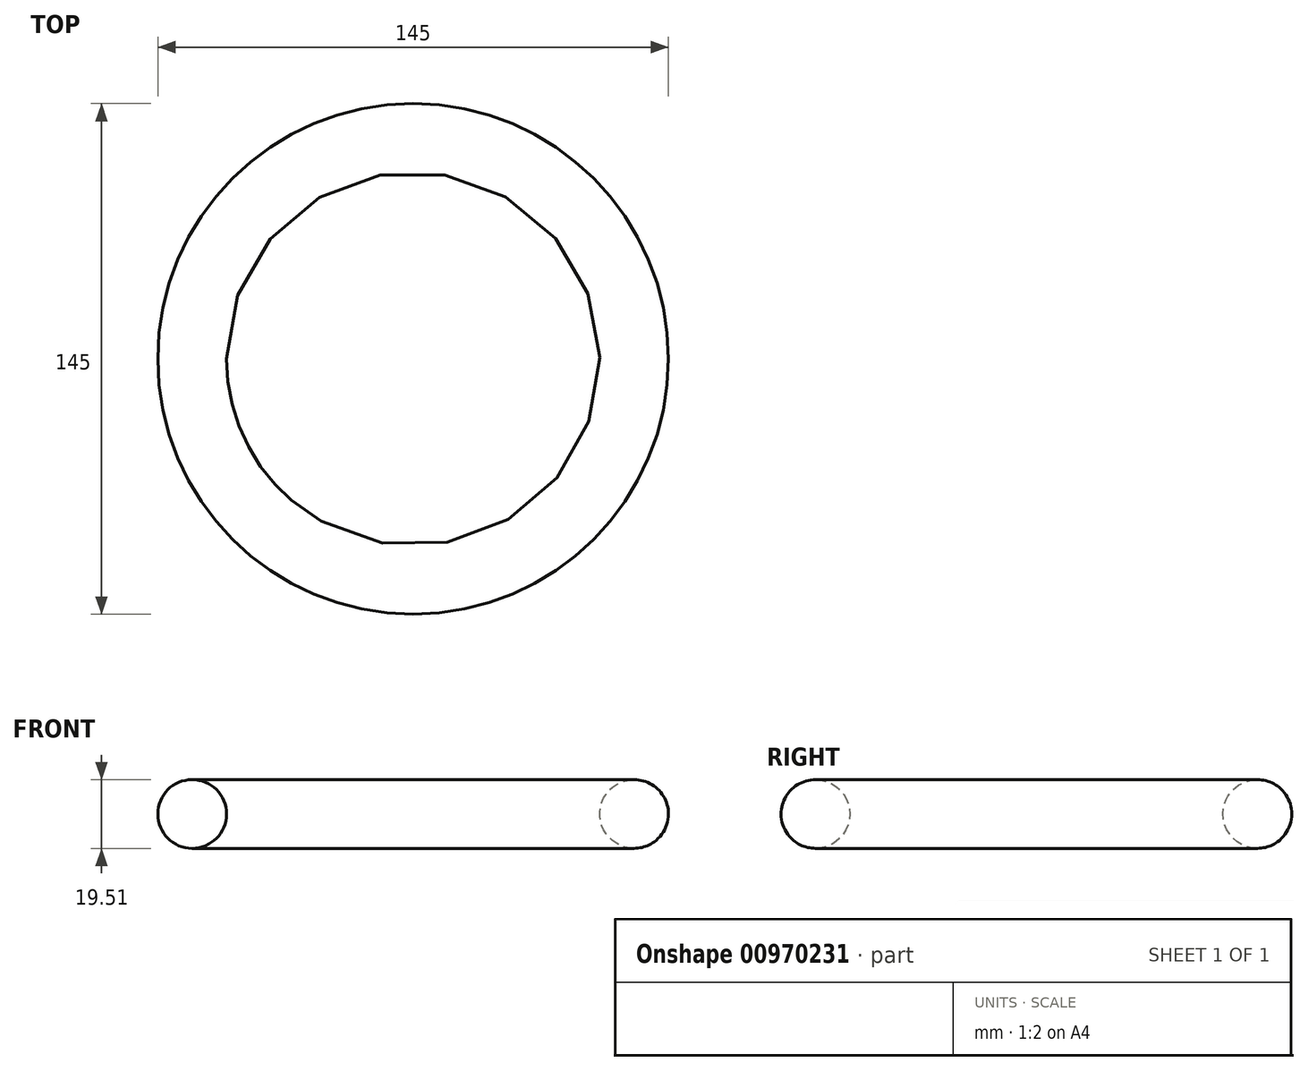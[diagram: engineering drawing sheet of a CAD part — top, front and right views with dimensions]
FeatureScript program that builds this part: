
annotation { "Feature Type Name" : "Feature", "Feature Type Description" : "" }
export const myFeature = defineFeature(function(context is Context, id is Id, definition is map)
    precondition{}
    {
        {
            var Q0;
            Q0=qCreatedBy(makeId("Front.planeOp"),FACE);
            var sketch = newSketch(context, id + "F0", { "sketchPlane" : qUnion([Q0])});
            skCircle(sketch, "E0", {"center": v(-62.75, 46.32) * mm, "radius": 9.76 * mm});
            skLineSegment(sketch, "E1", {"start": v(0, 0) * mm, "end": v(0, 60.48) * mm});
            skSolve(sketch);
        }
        {
            var Q0;
            Q0 = qSketchRegion(id + "F0", true);
            var Q1;
            Q1=sQuery(id+"F0.wireOp",EDGE,"E1");
            revolve(context, id + "F1", {"surfaceOperationType" : NewSurfaceOperationType.NEW, "entities" : qUnion([Q0]), "axis" : qUnion([Q1]), "revolveType" : RevolveType.FULL});
        }
    });
